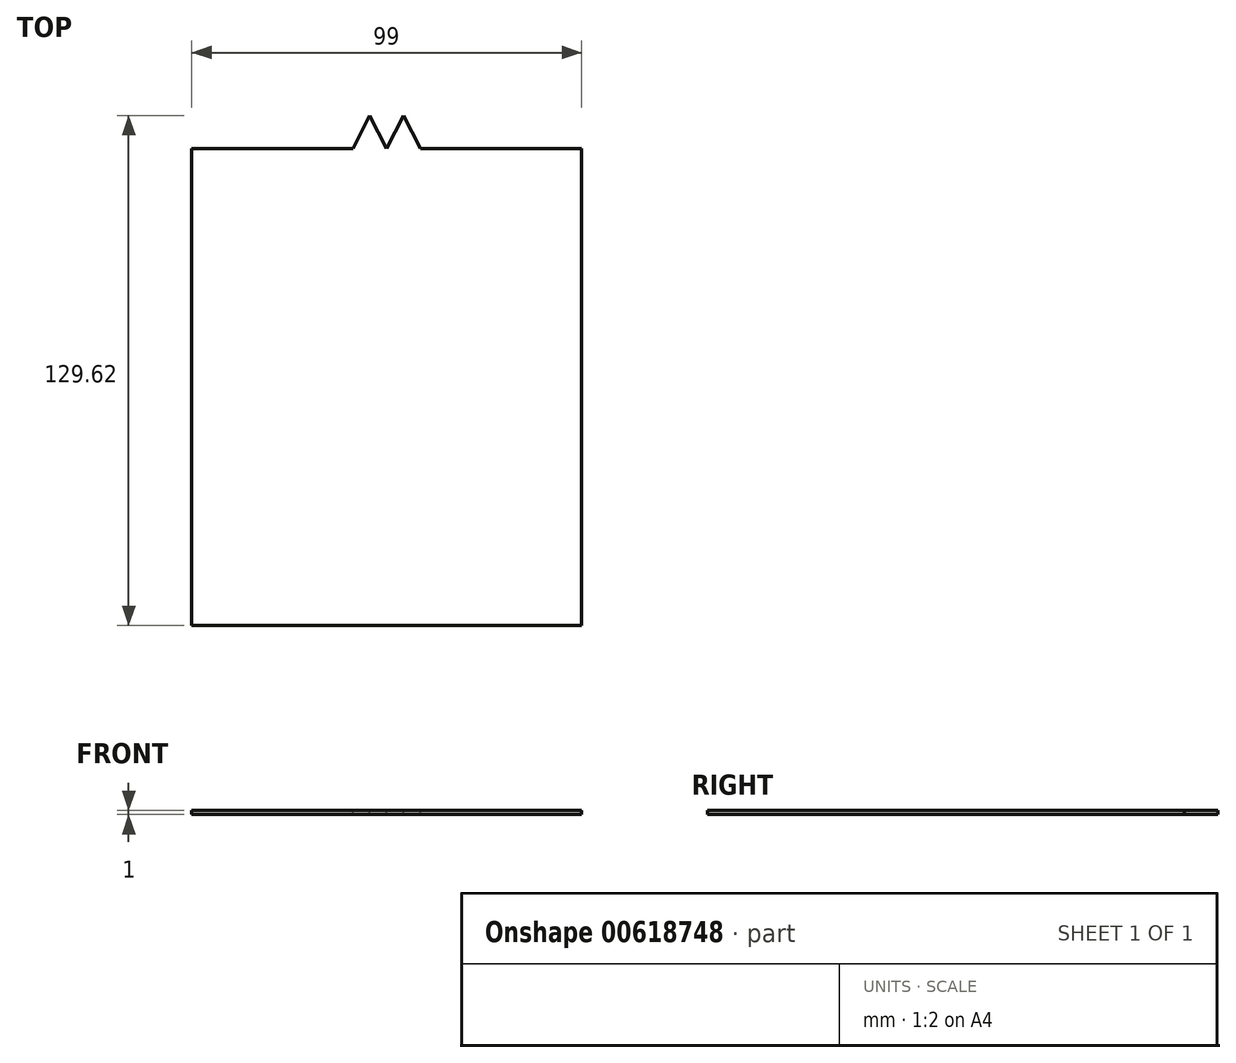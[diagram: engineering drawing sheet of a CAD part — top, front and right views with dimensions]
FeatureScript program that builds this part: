
annotation { "Feature Type Name" : "Feature", "Feature Type Description" : "" }
export const myFeature = defineFeature(function(context is Context, id is Id, definition is map)
    precondition{}
    {
        {
            var Q0;
            Q0=qCreatedBy(makeId("Top.planeOp"),FACE);
            var sketch = newSketch(context, id + "F0", { "sketchPlane" : qUnion([Q0])});
            skLineSegment(sketch, "E0.bottom", {"start": v(49.5, 75) * mm, "end": v(-49.5, 75) * mm});
            skLineSegment(sketch, "E0.top", {"start": v(49.5, -75) * mm, "end": v(-49.5, -75) * mm});
            skLineSegment(sketch, "E0.left", {"start": v(49.5, 75) * mm, "end": v(49.5, -75) * mm});
            skLineSegment(sketch, "E0.right", {"start": v(-49.5, 75) * mm, "end": v(-49.5, -75) * mm});
            skPoint(sketch, "E0.middle", {"position": v(0, 0) * mm});
            skSolve(sketch);
        }
        {
            var Q0;
            Q0=makeQuery(id+"F0.imprint","IMPRINT",FACE,{"disambiguationData":[TD([[makeQuery(id+"F0.imprint","IMPRINT",EDGE,{"derivedFrom":sQuery(id+"F0.wireOp",EDGE,"E0.bottom")}),1.0]])]});
            extrude(context, id + "F1", {"entities" : qUnion([Q0]), "depth" : 1 * mm, "offsetDistance" : 25 * mm});
        }
        {
            var Q0;
            Q0=makeQuery(id+"F1.opExtrude","CAP_FACE",FACE,{"disambiguationData":[OSD([sQuery(id+"F0.wireOp",EDGE,"E0.bottom"),sQuery(id+"F0.wireOp",EDGE,"E0.top"),sQuery(id+"F0.wireOp",EDGE,"E0.left"),sQuery(id+"F0.wireOp",EDGE,"E0.right")])],"isStart":false});
            var sketch = newSketch(context, id + "F2", { "sketchPlane" : qUnion([Q0])});
            skSolve(sketch);
        }
        {
            var Q0;
            Q0=makeQuery(id+"F2.imprint","IMPRINT",FACE,{"disambiguationData":[TD([[makeQuery(id+"F2.imprint","IMPRINT",EDGE,{"derivedFrom":makeQuery(id+"F1.opExtrude","CAP_EDGE",EDGE,{"disambiguationData":[OSD([sQuery(id+"F0.wireOp",EDGE,"E0.bottom")])],"isStart":false})}),1.0]])]});
            var sketch = newSketch(context, id + "F3", { "sketchPlane" : qUnion([Q0])});
            skLineSegment(sketch, "E1", {"start": v(-46.32, 46.22) * mm, "end": v(-8.58, 46.22) * mm});
            skLineSegment(sketch, "E2", {"start": v(-8.58, 46.22) * mm, "end": v(-4.3, 54.62) * mm});
            skLineSegment(sketch, "E3", {"start": v(-4.3, 54.62) * mm, "end": v(0, 46.22) * mm});
            skLineSegment(sketch, "E4", {"start": v(0, 46.22) * mm, "end": v(4.3, 54.62) * mm});
            skLineSegment(sketch, "E5", {"start": v(4.3, 54.62) * mm, "end": v(8.58, 46.22) * mm});
            skLineSegment(sketch, "E6", {"start": v(8.58, 46.22) * mm, "end": v(46.32, 46.22) * mm});
            skLineSegment(sketch, "E7", {"start": v(-46.32, 46.22) * mm, "end": v(-62, 46.22) * mm});
            skLineSegment(sketch, "E8", {"start": v(-62, 46.22) * mm, "end": v(-51.67, 77.81) * mm});
            skLineSegment(sketch, "E9", {"start": v(-51.67, 77.81) * mm, "end": v(59.02, 77.81) * mm});
            skLineSegment(sketch, "E10", {"start": v(59.02, 77.81) * mm, "end": v(54.14, 46.22) * mm});
            skLineSegment(sketch, "E11", {"start": v(54.14, 46.22) * mm, "end": v(46.32, 46.22) * mm});
            skPoint(sketch, "E12.right.end.orphan", {"position": v(8.44, -37.62) * mm});
            skPoint(sketch, "E13.top.end.orphan", {"position": v(35.16, -37.62) * mm});
            skSolve(sketch);
        }
        {
            var Q0;
            Q0 = qSketchRegion(id + "F3", true);
            extrude(context, id + "F4", {"entities" : qUnion([Q0]), "operationType" : NewBodyOperationType.REMOVE, "oppositeDirection" : true, "depth" : 25 * mm, "offsetDistance" : 25 * mm});
        }
    });
